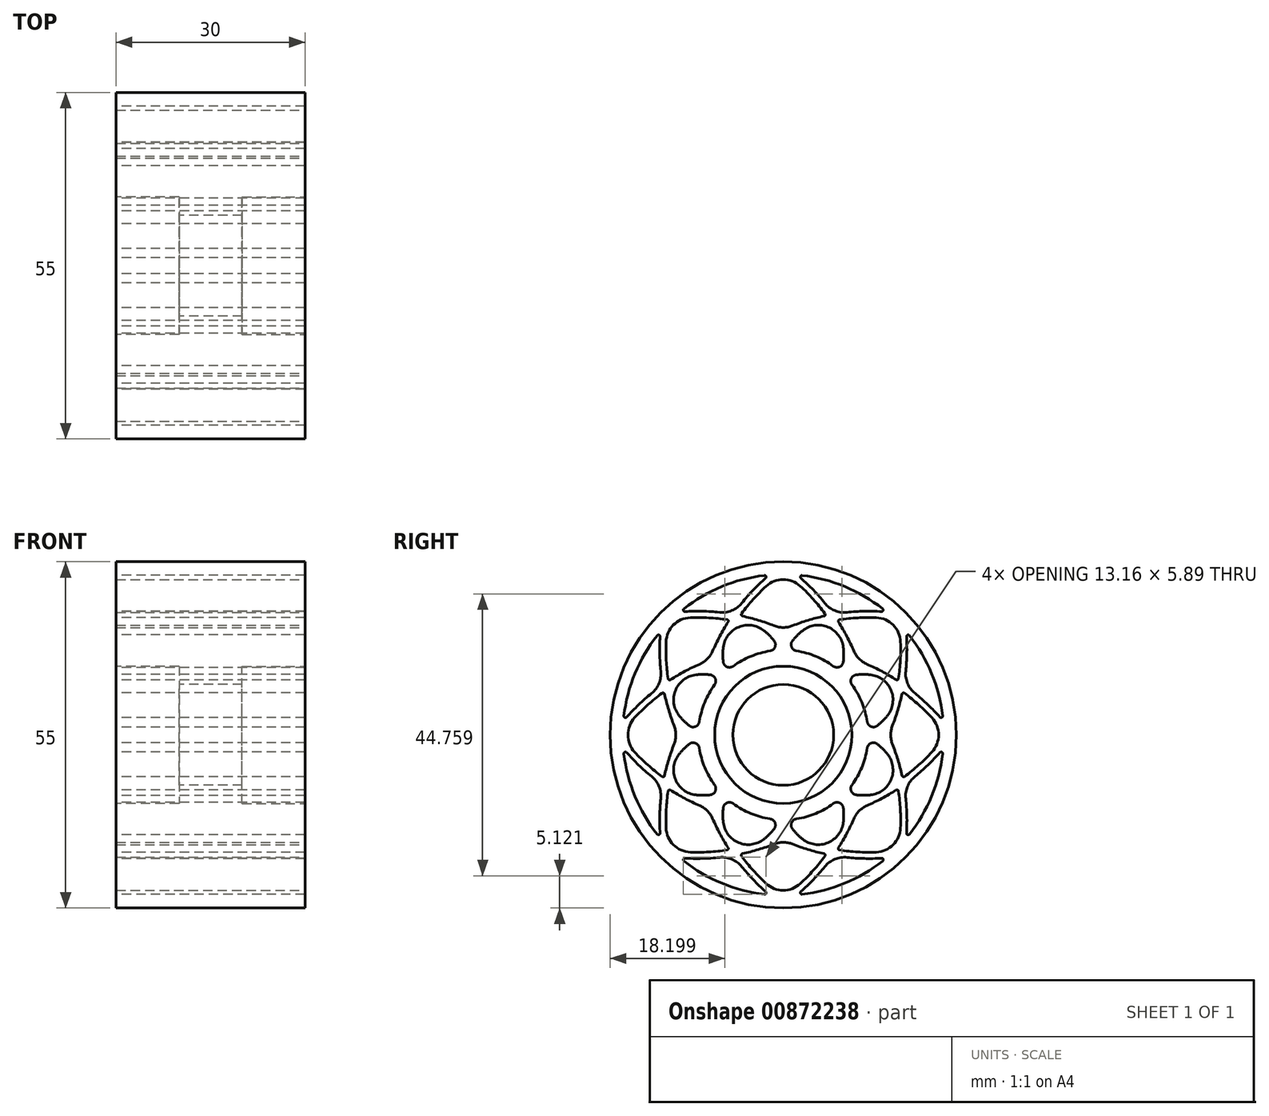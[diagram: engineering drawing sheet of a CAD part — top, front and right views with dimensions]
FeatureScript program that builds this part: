
annotation { "Feature Type Name" : "Feature", "Feature Type Description" : "" }
export const myFeature = defineFeature(function(context is Context, id is Id, definition is map)
    precondition{}
    {
        {
            var Q0;
            Q0=qCreatedBy(makeId("Right.planeOp"),FACE);
            var sketch = newSketch(context, id + "F0", { "sketchPlane" : qUnion([Q0])});
            skCircle(sketch, "E0", {"center": v(0, 0) * mm, "radius": 26.5 * mm, "construction": true});
            skCircle(sketch, "E1", {"center": v(0, 0) * mm, "radius": 13.5 * mm, "construction": true});
            skCircle(sketch, "E2", {"center": v(0, 0) * mm, "radius": 8 * mm});
            skArc(sketch, "E3", {"start": v(0, -26.5) * mm, "mid": v(13.5, 0) * mm, "end": v(0, 26.5) * mm, "construction": true});
            skArc(sketch, "E4", {"start": v(0, 26.5) * mm, "mid": v(-13.5, 0) * mm, "end": v(0, -26.5) * mm, "construction": true});
            skArc(sketch, "E5", {"start": v(26.5, 0) * mm, "mid": v(0, 13.5) * mm, "end": v(-26.5, 0) * mm, "construction": true});
            skArc(sketch, "E6", {"start": v(-26.5, 0) * mm, "mid": v(0, -13.5) * mm, "end": v(26.5, 0) * mm, "construction": true});
            skArc(sketch, "E7", {"start": v(18.74, -18.74) * mm, "mid": v(9.55, 9.55) * mm, "end": v(-18.74, 18.74) * mm, "construction": true});
            skArc(sketch, "E8", {"start": v(-18.74, 18.74) * mm, "mid": v(-9.55, -9.55) * mm, "end": v(18.74, -18.74) * mm, "construction": true});
            skArc(sketch, "E9", {"start": v(-18.74, -18.74) * mm, "mid": v(9.55, -9.55) * mm, "end": v(18.74, 18.74) * mm, "construction": true});
            skArc(sketch, "E10", {"start": v(18.74, 18.74) * mm, "mid": v(-9.55, 9.55) * mm, "end": v(-18.74, -18.74) * mm, "construction": true});
            skLineSegment(sketch, "E11", {"start": v(0, 26.5) * mm, "end": v(0, -26.5) * mm, "construction": true});
            skLineSegment(sketch, "E12", {"start": v(18.74, 18.74) * mm, "end": v(-18.74, -18.74) * mm, "construction": true});
            skLineSegment(sketch, "E13", {"start": v(-26.5, 0) * mm, "end": v(26.5, 0) * mm, "construction": true});
            skLineSegment(sketch, "E14", {"start": v(-18.74, 18.74) * mm, "end": v(18.74, -18.74) * mm, "construction": true});
            skCircle(sketch, "E15", {"center": v(0, 0) * mm, "radius": 27.5 * mm});
            skArc(sketch, "E16", {"start": v(-2.2, 25.4) * mm, "mid": v(-5.27, 22.46) * mm, "end": v(-7.93, 19.15) * mm});
            skArc(sketch, "E17", {"start": v(-7.93, 19.15) * mm, "mid": v(-12.16, 19.6) * mm, "end": v(-16.4, 19.52) * mm});
            skArc(sketch, "E18", {"start": v(7.93, 19.15) * mm, "mid": v(5.27, 22.46) * mm, "end": v(2.2, 25.4) * mm});
            skArc(sketch, "E19", {"start": v(18.3, 18.3) * mm, "mid": v(13.42, 18.64) * mm, "end": v(8.55, 18.24) * mm});
            skArc(sketch, "E20", {"start": v(11.83, 11.83) * mm, "mid": v(10.36, 15.12) * mm, "end": v(8.55, 18.24) * mm});
            skArc(sketch, "E21", {"start": v(-19.15, 7.93) * mm, "mid": v(-22.46, 5.27) * mm, "end": v(-25.4, 2.2) * mm});
            skArc(sketch, "E22", {"start": v(-19.52, 16.4) * mm, "mid": v(-19.6, 12.16) * mm, "end": v(-19.15, 7.93) * mm});
            skArc(sketch, "E23", {"start": v(19.15, 7.93) * mm, "mid": v(19.6, 12.16) * mm, "end": v(19.52, 16.4) * mm});
            skCircle(sketch, "E24", {"center": v(0, 0) * mm, "radius": 10.9 * mm});
            skArc(sketch, "E25", {"start": v(7.7, 18.6) * mm, "mid": v(3.5, 16.89) * mm, "end": v(0.5, 13.5) * mm});
            skArc(sketch, "E26", {"start": v(9.19, 9.9) * mm, "mid": v(9.46, 14.42) * mm, "end": v(7.7, 18.6) * mm});
            skArc(sketch, "E27", {"start": v(9.19, 9.9) * mm, "mid": v(5.17, 12.47) * mm, "end": v(0.5, 13.5) * mm});
            skArc(sketch, "E28", {"start": v(13.5, 0.5) * mm, "mid": v(16.89, 3.5) * mm, "end": v(18.6, 7.7) * mm});
            skArc(sketch, "E29", {"start": v(18.6, 7.7) * mm, "mid": v(14.42, 9.46) * mm, "end": v(9.9, 9.19) * mm});
            skArc(sketch, "E30", {"start": v(13.5, 0.5) * mm, "mid": v(12.47, 5.17) * mm, "end": v(9.9, 9.19) * mm});
            skArc(sketch, "E31", {"start": v(-18.95, 6.85) * mm, "mid": v(-22.67, 3.69) * mm, "end": v(-25.88, 0) * mm});
            skArc(sketch, "E32", {"start": v(-25.88, 0) * mm, "mid": v(-22.67, -3.69) * mm, "end": v(-18.95, -6.85) * mm});
            skArc(sketch, "E33", {"start": v(-16.72, 0) * mm, "mid": v(-18.02, -3.37) * mm, "end": v(-18.95, -6.85) * mm});
            skArc(sketch, "E34", {"start": v(25.88, 0) * mm, "mid": v(22.67, 3.69) * mm, "end": v(18.95, 6.85) * mm});
            skArc(sketch, "E35", {"start": v(16.72, 0) * mm, "mid": v(18.02, 3.37) * mm, "end": v(18.95, 6.85) * mm});
            skArc(sketch, "E36", {"start": v(-25.4, -2.2) * mm, "mid": v(-22.46, -5.27) * mm, "end": v(-19.15, -7.93) * mm});
            skArc(sketch, "E37", {"start": v(-19.15, -7.93) * mm, "mid": v(-19.6, -12.16) * mm, "end": v(-19.52, -16.4) * mm});
            skArc(sketch, "E38", {"start": v(19.15, -7.93) * mm, "mid": v(22.46, -5.27) * mm, "end": v(25.4, -2.2) * mm});
            skArc(sketch, "E39", {"start": v(19.52, -16.4) * mm, "mid": v(19.6, -12.16) * mm, "end": v(19.15, -7.93) * mm});
            skArc(sketch, "E40", {"start": v(11.83, -11.83) * mm, "mid": v(15.12, -10.36) * mm, "end": v(18.24, -8.55) * mm});
            skArc(sketch, "E41", {"start": v(18.3, -18.3) * mm, "mid": v(18.64, -13.42) * mm, "end": v(18.24, -8.55) * mm});
            skArc(sketch, "E42", {"start": v(-18.3, 18.3) * mm, "mid": v(-18.64, 13.42) * mm, "end": v(-18.24, 8.55) * mm});
            skArc(sketch, "E43", {"start": v(-8.55, 18.24) * mm, "mid": v(-10.36, 15.12) * mm, "end": v(-11.83, 11.83) * mm});
            skArc(sketch, "E44", {"start": v(-8.55, 18.24) * mm, "mid": v(-13.42, 18.64) * mm, "end": v(-18.3, 18.3) * mm});
            skArc(sketch, "E45", {"start": v(-13.5, -0.5) * mm, "mid": v(-16.89, -3.5) * mm, "end": v(-18.6, -7.7) * mm});
            skArc(sketch, "E46", {"start": v(-18.6, -7.7) * mm, "mid": v(-14.42, -9.46) * mm, "end": v(-9.9, -9.19) * mm});
            skArc(sketch, "E47", {"start": v(-18.6, 7.7) * mm, "mid": v(-16.89, 3.5) * mm, "end": v(-13.5, 0.5) * mm});
            skArc(sketch, "E48", {"start": v(-9.9, 9.19) * mm, "mid": v(-14.42, 9.46) * mm, "end": v(-18.6, 7.7) * mm});
            skArc(sketch, "E49", {"start": v(-0.5, 13.5) * mm, "mid": v(-3.5, 16.89) * mm, "end": v(-7.7, 18.6) * mm});
            skArc(sketch, "E50", {"start": v(-7.7, 18.6) * mm, "mid": v(-9.46, 14.42) * mm, "end": v(-9.19, 9.9) * mm});
            skArc(sketch, "E51", {"start": v(-0.5, 13.5) * mm, "mid": v(-5.17, 12.47) * mm, "end": v(-9.19, 9.9) * mm});
            skArc(sketch, "E52", {"start": v(0.5, -13.5) * mm, "mid": v(3.5, -16.89) * mm, "end": v(7.7, -18.6) * mm});
            skArc(sketch, "E53", {"start": v(7.7, -18.6) * mm, "mid": v(9.46, -14.42) * mm, "end": v(9.19, -9.9) * mm});
            skArc(sketch, "E54", {"start": v(0.5, -13.5) * mm, "mid": v(5.17, -12.47) * mm, "end": v(9.19, -9.9) * mm});
            skArc(sketch, "E55", {"start": v(-9.9, 9.19) * mm, "mid": v(-12.47, 5.17) * mm, "end": v(-13.5, 0.5) * mm});
            skArc(sketch, "E56", {"start": v(-9.19, -9.9) * mm, "mid": v(-9.46, -14.42) * mm, "end": v(-7.7, -18.6) * mm});
            skArc(sketch, "E57", {"start": v(-9.19, -9.9) * mm, "mid": v(-5.17, -12.47) * mm, "end": v(-0.5, -13.5) * mm});
            skArc(sketch, "E58", {"start": v(18.6, -7.7) * mm, "mid": v(16.89, -3.5) * mm, "end": v(13.5, -0.5) * mm});
            skArc(sketch, "E59", {"start": v(9.9, -9.19) * mm, "mid": v(14.42, -9.46) * mm, "end": v(18.6, -7.7) * mm});
            skArc(sketch, "E60", {"start": v(9.9, -9.19) * mm, "mid": v(12.47, -5.17) * mm, "end": v(13.5, -0.5) * mm});
            skArc(sketch, "E61", {"start": v(-7.7, -18.6) * mm, "mid": v(-3.5, -16.89) * mm, "end": v(-0.5, -13.5) * mm});
            skArc(sketch, "E62", {"start": v(-18.95, 6.85) * mm, "mid": v(-18.02, 3.37) * mm, "end": v(-16.72, 0) * mm});
            skArc(sketch, "E63", {"start": v(-16.4, -19.52) * mm, "mid": v(-12.16, -19.6) * mm, "end": v(-7.93, -19.15) * mm});
            skArc(sketch, "E64", {"start": v(-7.93, -19.15) * mm, "mid": v(-5.27, -22.46) * mm, "end": v(-2.2, -25.4) * mm});
            skArc(sketch, "E65", {"start": v(-11.83, 11.83) * mm, "mid": v(-15.12, 10.36) * mm, "end": v(-18.24, 8.55) * mm});
            skArc(sketch, "E66", {"start": v(-18.24, -8.55) * mm, "mid": v(-15.12, -10.36) * mm, "end": v(-11.83, -11.83) * mm});
            skArc(sketch, "E67", {"start": v(-18.24, -8.55) * mm, "mid": v(-18.64, -13.42) * mm, "end": v(-18.3, -18.3) * mm});
            skArc(sketch, "E68", {"start": v(-18.3, -18.3) * mm, "mid": v(-13.42, -18.64) * mm, "end": v(-8.55, -18.24) * mm});
            skArc(sketch, "E69", {"start": v(-11.83, -11.83) * mm, "mid": v(-10.36, -15.12) * mm, "end": v(-8.55, -18.24) * mm});
            skArc(sketch, "E70", {"start": v(-6.85, -18.95) * mm, "mid": v(-3.37, -18.02) * mm, "end": v(0, -16.72) * mm});
            skArc(sketch, "E71", {"start": v(-6.85, -18.95) * mm, "mid": v(-3.69, -22.67) * mm, "end": v(0, -25.88) * mm});
            skArc(sketch, "E72", {"start": v(0, -16.72) * mm, "mid": v(3.37, -18.02) * mm, "end": v(6.85, -18.95) * mm});
            skArc(sketch, "E73", {"start": v(0, -25.88) * mm, "mid": v(3.69, -22.67) * mm, "end": v(6.85, -18.95) * mm});
            skArc(sketch, "E74", {"start": v(2.2, -25.4) * mm, "mid": v(5.27, -22.46) * mm, "end": v(7.93, -19.15) * mm});
            skArc(sketch, "E75", {"start": v(7.93, -19.15) * mm, "mid": v(12.16, -19.6) * mm, "end": v(16.4, -19.52) * mm});
            skArc(sketch, "E76", {"start": v(0, 25.88) * mm, "mid": v(-3.69, 22.67) * mm, "end": v(-6.85, 18.95) * mm});
            skArc(sketch, "E77", {"start": v(0, 16.72) * mm, "mid": v(-3.37, 18.02) * mm, "end": v(-6.85, 18.95) * mm});
            skArc(sketch, "E78", {"start": v(6.85, 18.95) * mm, "mid": v(3.69, 22.67) * mm, "end": v(0, 25.88) * mm});
            skArc(sketch, "E79", {"start": v(6.85, 18.95) * mm, "mid": v(3.37, 18.02) * mm, "end": v(0, 16.72) * mm});
            skArc(sketch, "E80", {"start": v(18.24, 8.55) * mm, "mid": v(15.12, 10.36) * mm, "end": v(11.83, 11.83) * mm});
            skArc(sketch, "E81", {"start": v(18.24, 8.55) * mm, "mid": v(18.64, 13.42) * mm, "end": v(18.3, 18.3) * mm});
            skArc(sketch, "E82", {"start": v(18.95, -6.85) * mm, "mid": v(22.67, -3.69) * mm, "end": v(25.88, 0) * mm});
            skArc(sketch, "E83", {"start": v(18.95, -6.85) * mm, "mid": v(18.02, -3.37) * mm, "end": v(16.72, 0) * mm});
            skArc(sketch, "E84", {"start": v(8.55, -18.24) * mm, "mid": v(10.36, -15.12) * mm, "end": v(11.83, -11.83) * mm});
            skArc(sketch, "E85", {"start": v(8.55, -18.24) * mm, "mid": v(13.42, -18.64) * mm, "end": v(18.3, -18.3) * mm});
            skArc(sketch, "E86", {"start": v(-13.5, -0.5) * mm, "mid": v(-12.47, -5.17) * mm, "end": v(-9.9, -9.19) * mm});
            skArc(sketch, "E87", {"start": v(-19.52, 16.4) * mm, "mid": v(-23.56, 9.76) * mm, "end": v(-25.4, 2.2) * mm});
            skCircle(sketch, "E88", {"center": v(0, 0) * mm, "radius": 25.5 * mm, "construction": true});
            skArc(sketch, "E89", {"start": v(-2.2, 25.4) * mm, "mid": v(-9.76, 23.56) * mm, "end": v(-16.4, 19.52) * mm});
            skArc(sketch, "E90", {"start": v(25.4, 2.2) * mm, "mid": v(22.46, 5.27) * mm, "end": v(19.15, 7.93) * mm});
            skArc(sketch, "E91", {"start": v(25.4, 2.2) * mm, "mid": v(23.56, 9.76) * mm, "end": v(19.52, 16.4) * mm});
            skArc(sketch, "E92", {"start": v(16.4, 19.52) * mm, "mid": v(12.16, 19.6) * mm, "end": v(7.93, 19.15) * mm});
            skArc(sketch, "E93", {"start": v(16.4, 19.52) * mm, "mid": v(9.76, 23.56) * mm, "end": v(2.2, 25.4) * mm});
            skArc(sketch, "E94", {"start": v(-25.4, -2.2) * mm, "mid": v(-23.56, -9.76) * mm, "end": v(-19.52, -16.4) * mm});
            skArc(sketch, "E95", {"start": v(-16.4, -19.52) * mm, "mid": v(-9.76, -23.56) * mm, "end": v(-2.2, -25.4) * mm});
            skArc(sketch, "E96", {"start": v(2.2, -25.4) * mm, "mid": v(9.76, -23.56) * mm, "end": v(16.4, -19.52) * mm});
            skArc(sketch, "E97", {"start": v(19.52, -16.4) * mm, "mid": v(23.56, -9.76) * mm, "end": v(25.4, -2.2) * mm});
            skSolve(sketch);
        }
        {
            var Q0;
            Q0=makeQuery(id+"F0.imprint","IMPRINT",FACE,{"disambiguationData":[TD([[makeQuery(id+"F0.imprint","IMPRINT",EDGE,{"derivedFrom":sQuery(id+"F0.wireOp",EDGE,"E0")}),1.0]])]});
            var Q1;
            Q1=makeQuery(id+"F0.imprint","IMPRINT",FACE,{"disambiguationData":[TD([[makeQuery(id+"F0.imprint","IMPRINT",EDGE,{"derivedFrom":sQuery(id+"F0.wireOp",EDGE,"E2")}),-1.0]])]});
            var Q2;
            Q2=makeQuery(id+"F0.imprint","IMPRINT",FACE,{"disambiguationData":[TD([[makeQuery(id+"F0.imprint","IMPRINT",EDGE,{"derivedFrom":sQuery(id+"F0.wireOp",EDGE,"E15")}),1.0]])]});
            extrude(context, id + "F1", {"entities" : qUnion([Q0, Q1, Q2]), "flatOperationType" : FlatOperationType.REMOVE, "depth" : 30 * mm, "offsetDistance" : 25 * mm, "domain" : OperationDomain.MODEL, "symmetric" : true});
        }
        {
            var Q0;
            Q0=makeQuery(id+"F1.opExtrude","CAP_FACE",FACE,{"disambiguationData":[OSD([sQuery(id+"F0.wireOp",EDGE,"E0"),sQuery(id+"F0.wireOp",EDGE,"E2")])],"isStart":false});
            var sketch = newSketch(context, id + "F2", { "sketchPlane" : qUnion([Q0])});
            skCircle(sketch, "E98", {"center": v(0, 0) * mm, "radius": 10.9 * mm});
            skSolve(sketch);
        }
        {
            var Q0;
            Q0=makeQuery(id+"F2.imprint","IMPRINT",FACE,{"disambiguationData":[TD([[makeQuery(id+"F2.imprint","IMPRINT",EDGE,{"derivedFrom":makeQuery(id+"F1.opExtrude","CAP_EDGE",EDGE,{"disambiguationData":[OSD([sQuery(id+"F0.wireOp",EDGE,"E2")])],"isStart":false})}),1.0]])]});
            var Q1;
            Q1=makeQuery(id+"F2.imprint","IMPRINT",FACE,{"disambiguationData":[TD([[makeQuery(id+"F2.imprint","IMPRINT",EDGE,{"derivedFrom":sQuery(id+"F2.wireOp",EDGE,"E98")}),1.0]])]});
            extrude(context, id + "F3", {"entities" : qUnion([Q0, Q1]), "operationType" : NewBodyOperationType.REMOVE, "oppositeDirection" : true, "depth" : 10 * mm, "offsetDistance" : 25 * mm});
        }
        {
            var Q0;
            Q0=makeQuery(id+"F1.opExtrude","CAP_FACE",FACE,{"disambiguationData":[OSD([sQuery(id+"F0.wireOp",EDGE,"E0"),sQuery(id+"F0.wireOp",EDGE,"E2")])],"isStart":true});
            var sketch = newSketch(context, id + "F4", { "sketchPlane" : qUnion([Q0])});
            skCircle(sketch, "E99", {"center": v(0, 0) * mm, "radius": 10.9 * mm});
            skSolve(sketch);
        }
        {
            var Q0;
            Q0=makeQuery(id+"F4.imprint","IMPRINT",FACE,{"disambiguationData":[TD([[makeQuery(id+"F4.imprint","IMPRINT",EDGE,{"derivedFrom":makeQuery(id+"F1.opExtrude","CAP_EDGE",EDGE,{"disambiguationData":[OSD([sQuery(id+"F0.wireOp",EDGE,"E2")])],"isStart":true})}),1.0]])]});
            var Q1;
            Q1 = qConstructionFilter(qBodyType(qCreatedBy(id + "F4" ,EDGE), BodyType.WIRE), ConstructionObject.NO);
            var Q2;
            Q2=sQuery(id+"F0.wireOp",EDGE,"E2");
            extrude(context, id + "F5", {"entities" : qUnion([Q0]), "operationType" : NewBodyOperationType.REMOVE, "surfaceEntities" : qUnion([Q1, Q2]), "oppositeDirection" : true, "depth" : 10 * mm, "offsetDistance" : 25 * mm});
        }
        {
            var Q0;
            Q0=makeQuery(id+"F1.opExtrude","SWEPT_EDGE",EDGE,{"disambiguationData":[OSD([sQuery(id+"F0.wireOp",EDGE,"E16"),sQuery(id+"F0.wireOp",EDGE,"E17")])]});
            var Q1;
            Q1=makeQuery(id+"F1.opExtrude","SWEPT_EDGE",EDGE,{"disambiguationData":[OSD([sQuery(id+"F0.wireOp",EDGE,"E74"),sQuery(id+"F0.wireOp",EDGE,"E75")])]});
            var Q2;
            Q2=makeQuery(id+"F1.opExtrude","SWEPT_EDGE",EDGE,{"disambiguationData":[OSD([sQuery(id+"F0.wireOp",EDGE,"E63"),sQuery(id+"F0.wireOp",EDGE,"E64")])]});
            var Q3;
            Q3=makeQuery(id+"F1.opExtrude","SWEPT_EDGE",EDGE,{"disambiguationData":[OSD([sQuery(id+"F0.wireOp",EDGE,"E36"),sQuery(id+"F0.wireOp",EDGE,"E37")])]});
            var Q4;
            Q4=makeQuery(id+"F1.opExtrude","SWEPT_EDGE",EDGE,{"disambiguationData":[OSD([sQuery(id+"F0.wireOp",EDGE,"E21"),sQuery(id+"F0.wireOp",EDGE,"E22")])]});
            var Q5;
            Q5=makeQuery(id+"F1.opExtrude","SWEPT_EDGE",EDGE,{"disambiguationData":[OSD([sQuery(id+"F0.wireOp",EDGE,"E42"),sQuery(id+"F0.wireOp",EDGE,"E44")])]});
            var Q6;
            Q6=makeQuery(id+"F1.opExtrude","SWEPT_EDGE",EDGE,{"disambiguationData":[OSD([sQuery(id+"F0.wireOp",EDGE,"E49"),sQuery(id+"F0.wireOp",EDGE,"E50")])]});
            var Q7;
            Q7=makeQuery(id+"F1.opExtrude","SWEPT_EDGE",EDGE,{"disambiguationData":[OSD([sQuery(id+"F0.wireOp",EDGE,"E76"),sQuery(id+"F0.wireOp",EDGE,"E78")])]});
            var Q8;
            Q8=makeQuery(id+"F1.opExtrude","SWEPT_EDGE",EDGE,{"disambiguationData":[OSD([sQuery(id+"F0.wireOp",EDGE,"E77"),sQuery(id+"F0.wireOp",EDGE,"E79")])]});
            var Q9;
            Q9=makeQuery(id+"F1.opExtrude","SWEPT_EDGE",EDGE,{"disambiguationData":[OSD([sQuery(id+"F0.wireOp",EDGE,"E25"),sQuery(id+"F0.wireOp",EDGE,"E26")])]});
            var Q10;
            Q10=makeQuery(id+"F1.opExtrude","SWEPT_EDGE",EDGE,{"disambiguationData":[OSD([sQuery(id+"F0.wireOp",EDGE,"E19"),sQuery(id+"F0.wireOp",EDGE,"E81")])]});
            var Q11;
            Q11=makeQuery(id+"F1.opExtrude","SWEPT_EDGE",EDGE,{"disambiguationData":[OSD([sQuery(id+"F0.wireOp",EDGE,"E20"),sQuery(id+"F0.wireOp",EDGE,"E80")])]});
            var Q12;
            Q12=makeQuery(id+"F1.opExtrude","SWEPT_EDGE",EDGE,{"disambiguationData":[OSD([sQuery(id+"F0.wireOp",EDGE,"E28"),sQuery(id+"F0.wireOp",EDGE,"E29")])]});
            var Q13;
            Q13=makeQuery(id+"F1.opExtrude","SWEPT_EDGE",EDGE,{"disambiguationData":[OSD([sQuery(id+"F0.wireOp",EDGE,"E34"),sQuery(id+"F0.wireOp",EDGE,"E82")])]});
            var Q14;
            Q14=makeQuery(id+"F1.opExtrude","SWEPT_EDGE",EDGE,{"disambiguationData":[OSD([sQuery(id+"F0.wireOp",EDGE,"E35"),sQuery(id+"F0.wireOp",EDGE,"E83")])]});
            var Q15;
            Q15=makeQuery(id+"F1.opExtrude","SWEPT_EDGE",EDGE,{"disambiguationData":[OSD([sQuery(id+"F0.wireOp",EDGE,"E58"),sQuery(id+"F0.wireOp",EDGE,"E59")])]});
            var Q16;
            Q16=makeQuery(id+"F1.opExtrude","SWEPT_EDGE",EDGE,{"disambiguationData":[OSD([sQuery(id+"F0.wireOp",EDGE,"E40"),sQuery(id+"F0.wireOp",EDGE,"E84")])]});
            var Q17;
            Q17=makeQuery(id+"F1.opExtrude","SWEPT_EDGE",EDGE,{"disambiguationData":[OSD([sQuery(id+"F0.wireOp",EDGE,"E41"),sQuery(id+"F0.wireOp",EDGE,"E85")])]});
            var Q18;
            Q18=makeQuery(id+"F1.opExtrude","SWEPT_EDGE",EDGE,{"disambiguationData":[OSD([sQuery(id+"F0.wireOp",EDGE,"E52"),sQuery(id+"F0.wireOp",EDGE,"E53")])]});
            var Q19;
            Q19=makeQuery(id+"F1.opExtrude","SWEPT_EDGE",EDGE,{"disambiguationData":[OSD([sQuery(id+"F0.wireOp",EDGE,"E71"),sQuery(id+"F0.wireOp",EDGE,"E73")])]});
            var Q20;
            Q20=makeQuery(id+"F1.opExtrude","SWEPT_EDGE",EDGE,{"disambiguationData":[OSD([sQuery(id+"F0.wireOp",EDGE,"E70"),sQuery(id+"F0.wireOp",EDGE,"E72")])]});
            var Q21;
            Q21=makeQuery(id+"F1.opExtrude","SWEPT_EDGE",EDGE,{"disambiguationData":[OSD([sQuery(id+"F0.wireOp",EDGE,"E56"),sQuery(id+"F0.wireOp",EDGE,"E61")])]});
            var Q22;
            Q22=makeQuery(id+"F1.opExtrude","SWEPT_EDGE",EDGE,{"disambiguationData":[OSD([sQuery(id+"F0.wireOp",EDGE,"E66"),sQuery(id+"F0.wireOp",EDGE,"E69")])]});
            var Q23;
            Q23=makeQuery(id+"F1.opExtrude","SWEPT_EDGE",EDGE,{"disambiguationData":[OSD([sQuery(id+"F0.wireOp",EDGE,"E67"),sQuery(id+"F0.wireOp",EDGE,"E68")])]});
            var Q24;
            Q24=makeQuery(id+"F1.opExtrude","SWEPT_EDGE",EDGE,{"disambiguationData":[OSD([sQuery(id+"F0.wireOp",EDGE,"E45"),sQuery(id+"F0.wireOp",EDGE,"E46")])]});
            var Q25;
            Q25=makeQuery(id+"F1.opExtrude","SWEPT_EDGE",EDGE,{"disambiguationData":[OSD([sQuery(id+"F0.wireOp",EDGE,"E33"),sQuery(id+"F0.wireOp",EDGE,"E62")])]});
            var Q26;
            Q26=makeQuery(id+"F1.opExtrude","SWEPT_EDGE",EDGE,{"disambiguationData":[OSD([sQuery(id+"F0.wireOp",EDGE,"E31"),sQuery(id+"F0.wireOp",EDGE,"E32")])]});
            var Q27;
            Q27=makeQuery(id+"F1.opExtrude","SWEPT_EDGE",EDGE,{"disambiguationData":[OSD([sQuery(id+"F0.wireOp",EDGE,"E47"),sQuery(id+"F0.wireOp",EDGE,"E48")])]});
            var Q28;
            Q28=makeQuery(id+"F1.opExtrude","SWEPT_EDGE",EDGE,{"disambiguationData":[OSD([sQuery(id+"F0.wireOp",EDGE,"E43"),sQuery(id+"F0.wireOp",EDGE,"E65")])]});
            var Q29;
            Q29=makeQuery(id+"F1.opExtrude","SWEPT_EDGE",EDGE,{"disambiguationData":[OSD([sQuery(id+"F0.wireOp",EDGE,"E18"),sQuery(id+"F0.wireOp",EDGE,"E92")])]});
            var Q30;
            Q30=makeQuery(id+"F1.opExtrude","SWEPT_EDGE",EDGE,{"disambiguationData":[OSD([sQuery(id+"F0.wireOp",EDGE,"E23"),sQuery(id+"F0.wireOp",EDGE,"E90")])]});
            var Q31;
            Q31=makeQuery(id+"F1.opExtrude","SWEPT_EDGE",EDGE,{"disambiguationData":[OSD([sQuery(id+"F0.wireOp",EDGE,"E38"),sQuery(id+"F0.wireOp",EDGE,"E39")])]});
            fillet(context, id + "F6", {"entities" : qUnion([Q0, Q1, Q2, Q3, Q4, Q5, Q6, Q7, Q8, Q9, Q10, Q11, Q12, Q13, Q14, Q15, Q16, Q17, Q18, Q19, Q20, Q21, Q22, Q23, Q24, Q25, Q26, Q27, Q28, Q29, Q30, Q31]), "radius" : 4 * mm, "tangentPropagation" : true, "allowEdgeOverflow" : false});
        }
        {
            var Q0;
            Q0=makeQuery(id+"F1.opExtrude","SWEPT_EDGE",EDGE,{"disambiguationData":[OSD([sQuery(id+"F0.wireOp",EDGE,"E26"),sQuery(id+"F0.wireOp",EDGE,"E27")])]});
            var Q1;
            Q1=makeQuery(id+"F1.opExtrude","SWEPT_EDGE",EDGE,{"disambiguationData":[OSD([sQuery(id+"F0.wireOp",EDGE,"E29"),sQuery(id+"F0.wireOp",EDGE,"E30")])]});
            var Q2;
            Q2=makeQuery(id+"F1.opExtrude","SWEPT_EDGE",EDGE,{"disambiguationData":[OSD([sQuery(id+"F0.wireOp",EDGE,"E25"),sQuery(id+"F0.wireOp",EDGE,"E27")])]});
            var Q3;
            Q3=makeQuery(id+"F1.opExtrude","SWEPT_EDGE",EDGE,{"disambiguationData":[OSD([sQuery(id+"F0.wireOp",EDGE,"E49"),sQuery(id+"F0.wireOp",EDGE,"E51")])]});
            var Q4;
            Q4=makeQuery(id+"F1.opExtrude","SWEPT_EDGE",EDGE,{"disambiguationData":[OSD([sQuery(id+"F0.wireOp",EDGE,"E50"),sQuery(id+"F0.wireOp",EDGE,"E51")])]});
            var Q5;
            Q5=makeQuery(id+"F1.opExtrude","SWEPT_EDGE",EDGE,{"disambiguationData":[OSD([sQuery(id+"F0.wireOp",EDGE,"E48"),sQuery(id+"F0.wireOp",EDGE,"E55")])]});
            var Q6;
            Q6=makeQuery(id+"F1.opExtrude","SWEPT_EDGE",EDGE,{"disambiguationData":[OSD([sQuery(id+"F0.wireOp",EDGE,"E47"),sQuery(id+"F0.wireOp",EDGE,"E55")])]});
            var Q7;
            Q7=makeQuery(id+"F1.opExtrude","SWEPT_EDGE",EDGE,{"disambiguationData":[OSD([sQuery(id+"F0.wireOp",EDGE,"E45"),sQuery(id+"F0.wireOp",EDGE,"E86")])]});
            var Q8;
            Q8=makeQuery(id+"F1.opExtrude","SWEPT_EDGE",EDGE,{"disambiguationData":[OSD([sQuery(id+"F0.wireOp",EDGE,"E46"),sQuery(id+"F0.wireOp",EDGE,"E86")])]});
            var Q9;
            Q9=makeQuery(id+"F1.opExtrude","SWEPT_EDGE",EDGE,{"disambiguationData":[OSD([sQuery(id+"F0.wireOp",EDGE,"E56"),sQuery(id+"F0.wireOp",EDGE,"E57")])]});
            var Q10;
            Q10=makeQuery(id+"F1.opExtrude","SWEPT_EDGE",EDGE,{"disambiguationData":[OSD([sQuery(id+"F0.wireOp",EDGE,"E57"),sQuery(id+"F0.wireOp",EDGE,"E61")])]});
            var Q11;
            Q11=makeQuery(id+"F1.opExtrude","SWEPT_EDGE",EDGE,{"disambiguationData":[OSD([sQuery(id+"F0.wireOp",EDGE,"E53"),sQuery(id+"F0.wireOp",EDGE,"E54")])]});
            var Q12;
            Q12=makeQuery(id+"F1.opExtrude","SWEPT_EDGE",EDGE,{"disambiguationData":[OSD([sQuery(id+"F0.wireOp",EDGE,"E52"),sQuery(id+"F0.wireOp",EDGE,"E54")])]});
            var Q13;
            Q13=makeQuery(id+"F1.opExtrude","SWEPT_EDGE",EDGE,{"disambiguationData":[OSD([sQuery(id+"F0.wireOp",EDGE,"E58"),sQuery(id+"F0.wireOp",EDGE,"E60")])]});
            var Q14;
            Q14=makeQuery(id+"F1.opExtrude","SWEPT_EDGE",EDGE,{"disambiguationData":[OSD([sQuery(id+"F0.wireOp",EDGE,"E59"),sQuery(id+"F0.wireOp",EDGE,"E60")])]});
            var Q15;
            Q15=makeQuery(id+"F1.opExtrude","SWEPT_EDGE",EDGE,{"disambiguationData":[OSD([sQuery(id+"F0.wireOp",EDGE,"E28"),sQuery(id+"F0.wireOp",EDGE,"E30")])]});
            fillet(context, id + "F7", {"entities" : qUnion([Q0, Q1, Q2, Q3, Q4, Q5, Q6, Q7, Q8, Q9, Q10, Q11, Q12, Q13, Q14, Q15]), "radius" : 1 * mm, "tangentPropagation" : true, "allowEdgeOverflow" : false});
        }
        {
            var Q0;
            Q0=makeQuery(id+"F1.opExtrude","SWEPT_EDGE",EDGE,{"disambiguationData":[OSD([sQuery(id+"F0.wireOp",EDGE,"E42"),sQuery(id+"F0.wireOp",EDGE,"E44")])]});
            var Q1;
            Q1=makeQuery(id+"F1.opExtrude","SWEPT_EDGE",EDGE,{"disambiguationData":[OSD([sQuery(id+"F0.wireOp",EDGE,"E16"),sQuery(id+"F0.wireOp",EDGE,"E89")])]});
            var Q2;
            Q2=makeQuery(id+"F1.opExtrude","SWEPT_EDGE",EDGE,{"disambiguationData":[OSD([sQuery(id+"F0.wireOp",EDGE,"E17"),sQuery(id+"F0.wireOp",EDGE,"E89")])]});
            var Q3;
            Q3=makeQuery(id+"F1.opExtrude","SWEPT_EDGE",EDGE,{"disambiguationData":[OSD([sQuery(id+"F0.wireOp",EDGE,"E16"),sQuery(id+"F0.wireOp",EDGE,"E17")])]});
            var Q4;
            Q4=makeQuery(id+"F1.opExtrude","SWEPT_EDGE",EDGE,{"disambiguationData":[OSD([sQuery(id+"F0.wireOp",EDGE,"E21"),sQuery(id+"F0.wireOp",EDGE,"E22")])]});
            var Q5;
            Q5=makeQuery(id+"F1.opExtrude","SWEPT_EDGE",EDGE,{"disambiguationData":[OSD([sQuery(id+"F0.wireOp",EDGE,"E47"),sQuery(id+"F0.wireOp",EDGE,"E48")])]});
            var Q6;
            Q6=makeQuery(id+"F1.opExtrude","SWEPT_EDGE",EDGE,{"disambiguationData":[OSD([sQuery(id+"F0.wireOp",EDGE,"E22"),sQuery(id+"F0.wireOp",EDGE,"E87")])]});
            var Q7;
            Q7=makeQuery(id+"F1.opExtrude","SWEPT_EDGE",EDGE,{"disambiguationData":[OSD([sQuery(id+"F0.wireOp",EDGE,"E21"),sQuery(id+"F0.wireOp",EDGE,"E87")])]});
            var Q8;
            Q8=makeQuery(id+"F1.opExtrude","SWEPT_EDGE",EDGE,{"disambiguationData":[OSD([sQuery(id+"F0.wireOp",EDGE,"E31"),sQuery(id+"F0.wireOp",EDGE,"E32")])]});
            var Q9;
            Q9=makeQuery(id+"F1.opExtrude","SWEPT_EDGE",EDGE,{"disambiguationData":[OSD([sQuery(id+"F0.wireOp",EDGE,"E31"),sQuery(id+"F0.wireOp",EDGE,"E62")])]});
            var Q10;
            Q10=makeQuery(id+"F1.opExtrude","SWEPT_EDGE",EDGE,{"disambiguationData":[OSD([sQuery(id+"F0.wireOp",EDGE,"E32"),sQuery(id+"F0.wireOp",EDGE,"E33")])]});
            var Q11;
            Q11=makeQuery(id+"F1.opExtrude","SWEPT_EDGE",EDGE,{"disambiguationData":[OSD([sQuery(id+"F0.wireOp",EDGE,"E36"),sQuery(id+"F0.wireOp",EDGE,"E94")])]});
            var Q12;
            Q12=makeQuery(id+"F1.opExtrude","SWEPT_EDGE",EDGE,{"disambiguationData":[OSD([sQuery(id+"F0.wireOp",EDGE,"E37"),sQuery(id+"F0.wireOp",EDGE,"E94")])]});
            var Q13;
            Q13=makeQuery(id+"F1.opExtrude","SWEPT_EDGE",EDGE,{"disambiguationData":[OSD([sQuery(id+"F0.wireOp",EDGE,"E68"),sQuery(id+"F0.wireOp",EDGE,"E69")])]});
            var Q14;
            Q14=makeQuery(id+"F1.opExtrude","SWEPT_EDGE",EDGE,{"disambiguationData":[OSD([sQuery(id+"F0.wireOp",EDGE,"E66"),sQuery(id+"F0.wireOp",EDGE,"E67")])]});
            var Q15;
            Q15=makeQuery(id+"F1.opExtrude","SWEPT_EDGE",EDGE,{"disambiguationData":[OSD([sQuery(id+"F0.wireOp",EDGE,"E72"),sQuery(id+"F0.wireOp",EDGE,"E73")])]});
            var Q16;
            Q16=makeQuery(id+"F1.opExtrude","SWEPT_EDGE",EDGE,{"disambiguationData":[OSD([sQuery(id+"F0.wireOp",EDGE,"E70"),sQuery(id+"F0.wireOp",EDGE,"E71")])]});
            var Q17;
            Q17=makeQuery(id+"F1.opExtrude","SWEPT_EDGE",EDGE,{"disambiguationData":[OSD([sQuery(id+"F0.wireOp",EDGE,"E63"),sQuery(id+"F0.wireOp",EDGE,"E95")])]});
            var Q18;
            Q18=makeQuery(id+"F1.opExtrude","SWEPT_EDGE",EDGE,{"disambiguationData":[OSD([sQuery(id+"F0.wireOp",EDGE,"E64"),sQuery(id+"F0.wireOp",EDGE,"E95")])]});
            var Q19;
            Q19=makeQuery(id+"F1.opExtrude","SWEPT_EDGE",EDGE,{"disambiguationData":[OSD([sQuery(id+"F0.wireOp",EDGE,"E74"),sQuery(id+"F0.wireOp",EDGE,"E96")])]});
            var Q20;
            Q20=makeQuery(id+"F1.opExtrude","SWEPT_EDGE",EDGE,{"disambiguationData":[OSD([sQuery(id+"F0.wireOp",EDGE,"E75"),sQuery(id+"F0.wireOp",EDGE,"E96")])]});
            var Q21;
            Q21=makeQuery(id+"F1.opExtrude","SWEPT_EDGE",EDGE,{"disambiguationData":[OSD([sQuery(id+"F0.wireOp",EDGE,"E40"),sQuery(id+"F0.wireOp",EDGE,"E41")])]});
            var Q22;
            Q22=makeQuery(id+"F1.opExtrude","SWEPT_EDGE",EDGE,{"disambiguationData":[OSD([sQuery(id+"F0.wireOp",EDGE,"E84"),sQuery(id+"F0.wireOp",EDGE,"E85")])]});
            var Q23;
            Q23=makeQuery(id+"F1.opExtrude","SWEPT_EDGE",EDGE,{"disambiguationData":[OSD([sQuery(id+"F0.wireOp",EDGE,"E39"),sQuery(id+"F0.wireOp",EDGE,"E97")])]});
            var Q24;
            Q24=makeQuery(id+"F1.opExtrude","SWEPT_EDGE",EDGE,{"disambiguationData":[OSD([sQuery(id+"F0.wireOp",EDGE,"E38"),sQuery(id+"F0.wireOp",EDGE,"E97")])]});
            var Q25;
            Q25=makeQuery(id+"F1.opExtrude","SWEPT_EDGE",EDGE,{"disambiguationData":[OSD([sQuery(id+"F0.wireOp",EDGE,"E82"),sQuery(id+"F0.wireOp",EDGE,"E83")])]});
            var Q26;
            Q26=makeQuery(id+"F1.opExtrude","SWEPT_EDGE",EDGE,{"disambiguationData":[OSD([sQuery(id+"F0.wireOp",EDGE,"E34"),sQuery(id+"F0.wireOp",EDGE,"E35")])]});
            var Q27;
            Q27=makeQuery(id+"F1.opExtrude","SWEPT_EDGE",EDGE,{"disambiguationData":[OSD([sQuery(id+"F0.wireOp",EDGE,"E90"),sQuery(id+"F0.wireOp",EDGE,"E91")])]});
            var Q28;
            Q28=makeQuery(id+"F1.opExtrude","SWEPT_EDGE",EDGE,{"disambiguationData":[OSD([sQuery(id+"F0.wireOp",EDGE,"E23"),sQuery(id+"F0.wireOp",EDGE,"E91")])]});
            var Q29;
            Q29=makeQuery(id+"F1.opExtrude","SWEPT_EDGE",EDGE,{"disambiguationData":[OSD([sQuery(id+"F0.wireOp",EDGE,"E80"),sQuery(id+"F0.wireOp",EDGE,"E81")])]});
            var Q30;
            Q30=makeQuery(id+"F1.opExtrude","SWEPT_EDGE",EDGE,{"disambiguationData":[OSD([sQuery(id+"F0.wireOp",EDGE,"E19"),sQuery(id+"F0.wireOp",EDGE,"E20")])]});
            var Q31;
            Q31=makeQuery(id+"F1.opExtrude","SWEPT_EDGE",EDGE,{"disambiguationData":[OSD([sQuery(id+"F0.wireOp",EDGE,"E78"),sQuery(id+"F0.wireOp",EDGE,"E79")])]});
            var Q32;
            Q32=makeQuery(id+"F1.opExtrude","SWEPT_EDGE",EDGE,{"disambiguationData":[OSD([sQuery(id+"F0.wireOp",EDGE,"E76"),sQuery(id+"F0.wireOp",EDGE,"E77")])]});
            var Q33;
            Q33=makeQuery(id+"F1.opExtrude","SWEPT_EDGE",EDGE,{"disambiguationData":[OSD([sQuery(id+"F0.wireOp",EDGE,"E18"),sQuery(id+"F0.wireOp",EDGE,"E93")])]});
            var Q34;
            Q34=makeQuery(id+"F1.opExtrude","SWEPT_EDGE",EDGE,{"disambiguationData":[OSD([sQuery(id+"F0.wireOp",EDGE,"E92"),sQuery(id+"F0.wireOp",EDGE,"E93")])]});
            var Q35;
            Q35=makeQuery(id+"F1.opExtrude","SWEPT_EDGE",EDGE,{"disambiguationData":[OSD([sQuery(id+"F0.wireOp",EDGE,"E43"),sQuery(id+"F0.wireOp",EDGE,"E44")])]});
            var Q36;
            Q36=makeQuery(id+"F1.opExtrude","SWEPT_EDGE",EDGE,{"disambiguationData":[OSD([sQuery(id+"F0.wireOp",EDGE,"E42"),sQuery(id+"F0.wireOp",EDGE,"E65")])]});
            fillet(context, id + "F8", {"entities" : qUnion([Q0, Q1, Q2, Q3, Q4, Q5, Q6, Q7, Q8, Q9, Q10, Q11, Q12, Q13, Q14, Q15, Q16, Q17, Q18, Q19, Q20, Q21, Q22, Q23, Q24, Q25, Q26, Q27, Q28, Q29, Q30, Q31, Q32, Q33, Q34, Q35, Q36]), "radius" : 0.25 * mm, "tangentPropagation" : true, "allowEdgeOverflow" : false});
        }
    });
